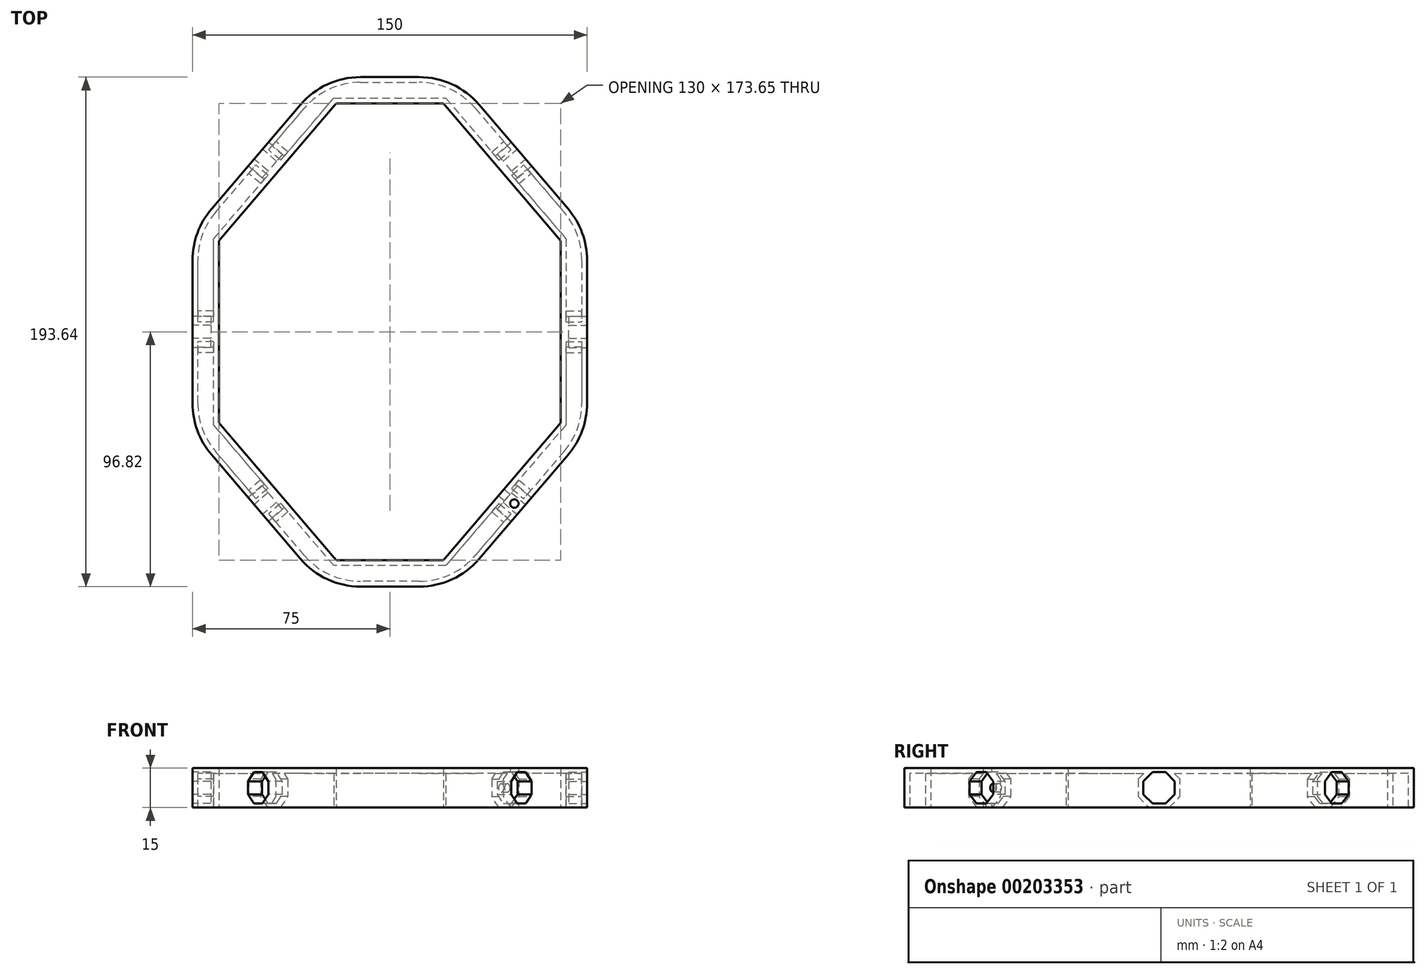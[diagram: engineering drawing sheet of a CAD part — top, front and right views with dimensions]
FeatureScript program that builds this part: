
annotation { "Feature Type Name" : "Feature", "Feature Type Description" : "" }
export const myFeature = defineFeature(function(context is Context, id is Id, definition is map)
    precondition{}
    {
        {
            var Q0;
            Q0=qCreatedBy(makeId("Front.planeOp"),FACE);
            var sketch = newSketch(context, id + "F0", { "sketchPlane" : qUnion([Q0])});
            skPoint(sketch, "E0.endSnap0", {"position": v(0, -12.85) * mm});
            skLineSegment(sketch, "E1", {"start": v(0, 12.85) * mm, "end": v(0, -12.85) * mm, "construction": true});
            skPoint(sketch, "E2", {"position": v(0, 0) * mm});
            skPoint(sketch, "E3", {"position": v(-5.95, 6.72) * mm});
            skPoint(sketch, "E4", {"position": v(-5.95, -6.72) * mm});
            skPoint(sketch, "E5", {"position": v(5.95, 6.72) * mm});
            skPoint(sketch, "E6", {"position": v(5.95, -6.72) * mm});
            skCircle(sketch, "E7.cCircle", {"center": v(0, 0) * mm, "radius": 9.7 * mm, "construction": true});
            skLineSegment(sketch, "E7.0", {"start": v(-8.96, 3.71) * mm, "end": v(-3.71, 8.96) * mm});
            skLineSegment(sketch, "E7.1", {"start": v(-3.71, 8.96) * mm, "end": v(3.71, 8.96) * mm});
            skLineSegment(sketch, "E7.2", {"start": v(3.71, 8.96) * mm, "end": v(8.96, 3.71) * mm});
            skLineSegment(sketch, "E7.3", {"start": v(8.96, 3.71) * mm, "end": v(8.96, -3.71) * mm});
            skLineSegment(sketch, "E7.4", {"start": v(8.96, -3.71) * mm, "end": v(3.71, -8.96) * mm});
            skLineSegment(sketch, "E7.5", {"start": v(3.71, -8.96) * mm, "end": v(-3.71, -8.96) * mm});
            skLineSegment(sketch, "E7.6", {"start": v(-3.71, -8.96) * mm, "end": v(-8.96, -3.71) * mm});
            skLineSegment(sketch, "E7.7", {"start": v(-8.96, -3.71) * mm, "end": v(-8.96, 3.71) * mm});
            skLineSegment(sketch, "E8.0", {"start": v(5.96, -2.47) * mm, "end": v(2.47, -5.96) * mm});
            skLineSegment(sketch, "E8.1", {"start": v(5.96, 2.47) * mm, "end": v(5.96, -2.47) * mm});
            skLineSegment(sketch, "E8.2", {"start": v(2.47, -5.96) * mm, "end": v(-2.47, -5.96) * mm});
            skLineSegment(sketch, "E8.3", {"start": v(2.47, 5.96) * mm, "end": v(5.96, 2.47) * mm});
            skLineSegment(sketch, "E8.4", {"start": v(-2.47, -5.96) * mm, "end": v(-5.96, -2.47) * mm});
            skLineSegment(sketch, "E8.5", {"start": v(-5.96, -2.47) * mm, "end": v(-5.96, 2.47) * mm});
            skLineSegment(sketch, "E8.6", {"start": v(-5.96, 2.47) * mm, "end": v(-2.47, 5.96) * mm});
            skLineSegment(sketch, "E8.7", {"start": v(-2.47, 5.96) * mm, "end": v(2.47, 5.96) * mm});
            skSolve(sketch);
        }
        {
            var Q0;
            Q0=qCreatedBy(makeId("Top.planeOp"),FACE);
            var sketch = newSketch(context, id + "F1", { "sketchPlane" : qUnion([Q0])});
            skLineSegment(sketch, "E9.0", {"start": v(-25, -96.82) * mm, "end": v(-75, -38.27) * mm});
            skLineSegment(sketch, "E9.1", {"start": v(-75, -38.27) * mm, "end": v(-75, 38.27) * mm});
            skLineSegment(sketch, "E9.2", {"start": v(-75, 38.27) * mm, "end": v(-25, 96.82) * mm});
            skLineSegment(sketch, "E9.3", {"start": v(-25, 96.82) * mm, "end": v(25, 96.82) * mm});
            skLineSegment(sketch, "E9.4", {"start": v(25, 96.82) * mm, "end": v(75, 38.27) * mm});
            skLineSegment(sketch, "E9.5", {"start": v(75, 38.27) * mm, "end": v(75, -38.27) * mm});
            skLineSegment(sketch, "E9.6", {"start": v(75, -38.27) * mm, "end": v(25, -96.82) * mm});
            skLineSegment(sketch, "E9.7", {"start": v(25, -96.82) * mm, "end": v(-25, -96.82) * mm});
            skLineSegment(sketch, "E10", {"start": v(0, 138.75) * mm, "end": v(0, -143.6) * mm, "construction": true});
            skPoint(sketch, "E11", {"position": v(0, 96.82) * mm});
            skPoint(sketch, "E12", {"position": v(0, -96.82) * mm});
            skLineSegment(sketch, "E13", {"start": v(-114.22, 0) * mm, "end": v(128.87, 0) * mm, "construction": true});
            skPoint(sketch, "E14", {"position": v(-75, 0) * mm});
            skPoint(sketch, "E15", {"position": v(75, 0) * mm});
            skLineSegment(sketch, "E16.0", {"start": v(65, 34.58) * mm, "end": v(65, -34.58) * mm});
            skLineSegment(sketch, "E16.1", {"start": v(20.39, 86.82) * mm, "end": v(65, 34.58) * mm});
            skLineSegment(sketch, "E16.2", {"start": v(65, -34.58) * mm, "end": v(20.39, -86.82) * mm});
            skLineSegment(sketch, "E16.3", {"start": v(-20.39, 86.82) * mm, "end": v(20.39, 86.82) * mm});
            skLineSegment(sketch, "E16.4", {"start": v(20.39, -86.82) * mm, "end": v(-20.39, -86.82) * mm});
            skLineSegment(sketch, "E16.5", {"start": v(-20.39, -86.82) * mm, "end": v(-65, -34.58) * mm});
            skLineSegment(sketch, "E16.6", {"start": v(-65, -34.58) * mm, "end": v(-65, 34.58) * mm});
            skLineSegment(sketch, "E16.7", {"start": v(-65, 34.58) * mm, "end": v(-20.39, 86.82) * mm});
            skSolve(sketch);
        }
        {
            var Q0;
            Q0=makeQuery(id+"F1.imprint","IMPRINT",FACE,{"disambiguationData":[TD([[makeQuery(id+"F1.imprint","IMPRINT",EDGE,{"derivedFrom":sQuery(id+"F1.wireOp",EDGE,"E9.0")}),-1.0]])]});
            extrude(context, id + "F2", {"entities" : qUnion([Q0]), "depth" : 15 * mm});
        }
        {
            var Q0;
            Q0=makeQuery(id+"F2.opExtrude","SWEPT_FACE",FACE,{"disambiguationData":[OSD([sQuery(id+"F1.wireOp",EDGE,"E9.4")])]});
            var sketch = newSketch(context, id + "F3", { "sketchPlane" : qUnion([Q0])});
            skPoint(sketch, "E17.endSnap0", {"position": v(18.9, 0) * mm});
            skLineSegment(sketch, "E18", {"start": v(18.9, 15) * mm, "end": v(18.9, 0) * mm, "construction": true});
            skPoint(sketch, "E19", {"position": v(18.9, 7.5) * mm});
            skPoint(sketch, "E20", {"position": v(12.95, 14.22) * mm});
            skPoint(sketch, "E21", {"position": v(12.94, 0.78) * mm});
            skPoint(sketch, "E22", {"position": v(24.85, 14.22) * mm});
            skPoint(sketch, "E23", {"position": v(24.85, 0.78) * mm});
            skCircle(sketch, "E24.cCircle", {"center": v(18.9, 7.5) * mm, "radius": 9.7 * mm, "construction": true});
            skLineSegment(sketch, "E24.0", {"start": v(9.94, 11.21) * mm, "end": v(15.19, 16.46) * mm});
            skLineSegment(sketch, "E24.1", {"start": v(15.19, 16.46) * mm, "end": v(22.61, 16.46) * mm});
            skLineSegment(sketch, "E24.2", {"start": v(22.61, 16.46) * mm, "end": v(27.86, 11.21) * mm});
            skLineSegment(sketch, "E24.3", {"start": v(27.86, 11.21) * mm, "end": v(27.86, 3.79) * mm});
            skLineSegment(sketch, "E24.4", {"start": v(27.86, 3.79) * mm, "end": v(22.61, -1.46) * mm});
            skLineSegment(sketch, "E24.5", {"start": v(22.61, -1.46) * mm, "end": v(15.19, -1.46) * mm});
            skLineSegment(sketch, "E24.6", {"start": v(15.19, -1.46) * mm, "end": v(9.94, 3.79) * mm});
            skLineSegment(sketch, "E24.7", {"start": v(9.94, 3.79) * mm, "end": v(9.94, 11.21) * mm});
            skLineSegment(sketch, "E25.0", {"start": v(24.86, 5.03) * mm, "end": v(21.37, 1.54) * mm});
            skLineSegment(sketch, "E25.1", {"start": v(24.86, 9.97) * mm, "end": v(24.86, 5.03) * mm});
            skLineSegment(sketch, "E25.2", {"start": v(21.37, 1.54) * mm, "end": v(16.43, 1.54) * mm});
            skLineSegment(sketch, "E25.3", {"start": v(21.37, 13.46) * mm, "end": v(24.86, 9.97) * mm});
            skLineSegment(sketch, "E25.4", {"start": v(16.43, 1.54) * mm, "end": v(12.94, 5.03) * mm});
            skLineSegment(sketch, "E25.5", {"start": v(12.94, 5.03) * mm, "end": v(12.94, 9.97) * mm});
            skLineSegment(sketch, "E25.6", {"start": v(12.94, 9.97) * mm, "end": v(16.43, 13.46) * mm});
            skLineSegment(sketch, "E25.7", {"start": v(16.43, 13.46) * mm, "end": v(21.37, 13.46) * mm});
            skSolve(sketch);
        }
        {
            var Q0;
            Q0=makeQuery(id+"F3.imprint","IMPRINT",FACE,{"disambiguationData":[TD([[makeQuery(id+"F3.imprint","IMPRINT",EDGE,{"derivedFrom":sQuery(id+"F3.wireOp",EDGE,"E25.0")}),-1.0]])]});
            extrude(context, id + "F4", {"entities" : qUnion([Q0]), "operationType" : NewBodyOperationType.REMOVE, "oppositeDirection" : true, "depth" : 7 * mm});
        }
        {
            var Q0;
            Q0=makeQuery(id+"F2.opExtrude","SWEPT_FACE",FACE,{"disambiguationData":[OSD([sQuery(id+"F1.wireOp",EDGE,"E9.5")])]});
            var sketch = newSketch(context, id + "F5", { "sketchPlane" : qUnion([Q0])});
            skPoint(sketch, "E26.endSnap0", {"position": v(0, 0) * mm});
            skLineSegment(sketch, "E27", {"start": v(0, 15) * mm, "end": v(0, 0) * mm, "construction": true});
            skPoint(sketch, "E28", {"position": v(0, 7.5) * mm});
            skPoint(sketch, "E29", {"position": v(-5.95, 14.22) * mm});
            skPoint(sketch, "E30", {"position": v(-5.95, 0.78) * mm});
            skPoint(sketch, "E31", {"position": v(5.95, 14.22) * mm});
            skPoint(sketch, "E32", {"position": v(5.95, 0.78) * mm});
            skCircle(sketch, "E33.cCircle", {"center": v(0, 7.5) * mm, "radius": 9.7 * mm, "construction": true});
            skLineSegment(sketch, "E33.0", {"start": v(-8.96, 11.21) * mm, "end": v(-3.71, 16.46) * mm});
            skLineSegment(sketch, "E33.1", {"start": v(-3.71, 16.46) * mm, "end": v(3.71, 16.46) * mm});
            skLineSegment(sketch, "E33.2", {"start": v(3.71, 16.46) * mm, "end": v(8.96, 11.21) * mm});
            skLineSegment(sketch, "E33.3", {"start": v(8.96, 11.21) * mm, "end": v(8.96, 3.79) * mm});
            skLineSegment(sketch, "E33.4", {"start": v(8.96, 3.79) * mm, "end": v(3.71, -1.46) * mm});
            skLineSegment(sketch, "E33.5", {"start": v(3.71, -1.46) * mm, "end": v(-3.71, -1.46) * mm});
            skLineSegment(sketch, "E33.6", {"start": v(-3.71, -1.46) * mm, "end": v(-8.96, 3.79) * mm});
            skLineSegment(sketch, "E33.7", {"start": v(-8.96, 3.79) * mm, "end": v(-8.96, 11.21) * mm});
            skLineSegment(sketch, "E34.0", {"start": v(5.96, 5.03) * mm, "end": v(2.47, 1.54) * mm});
            skLineSegment(sketch, "E34.1", {"start": v(5.96, 9.97) * mm, "end": v(5.96, 5.03) * mm});
            skLineSegment(sketch, "E34.2", {"start": v(2.47, 1.54) * mm, "end": v(-2.47, 1.54) * mm});
            skLineSegment(sketch, "E34.3", {"start": v(2.47, 13.46) * mm, "end": v(5.96, 9.97) * mm});
            skLineSegment(sketch, "E34.4", {"start": v(-2.47, 1.54) * mm, "end": v(-5.96, 5.03) * mm});
            skLineSegment(sketch, "E34.5", {"start": v(-5.96, 5.03) * mm, "end": v(-5.96, 9.97) * mm});
            skLineSegment(sketch, "E34.6", {"start": v(-5.96, 9.97) * mm, "end": v(-2.47, 13.46) * mm});
            skLineSegment(sketch, "E34.7", {"start": v(-2.47, 13.46) * mm, "end": v(2.47, 13.46) * mm});
            skSolve(sketch);
        }
        {
            var Q0;
            Q0=makeQuery(id+"F2.opExtrude","SWEPT_FACE",FACE,{"disambiguationData":[OSD([sQuery(id+"F1.wireOp",EDGE,"E9.6")])]});
            var sketch = newSketch(context, id + "F6", { "sketchPlane" : qUnion([Q0])});
            skPoint(sketch, "E35.endSnap0", {"position": v(-18.9, 0) * mm});
            skLineSegment(sketch, "E36", {"start": v(-18.9, 15) * mm, "end": v(-18.9, 0) * mm, "construction": true});
            skPoint(sketch, "E37", {"position": v(-18.9, 7.5) * mm});
            skPoint(sketch, "E38", {"position": v(-24.85, 14.22) * mm});
            skPoint(sketch, "E39", {"position": v(-24.85, 0.78) * mm});
            skPoint(sketch, "E40", {"position": v(-12.95, 14.22) * mm});
            skPoint(sketch, "E41", {"position": v(-12.95, 0.78) * mm});
            skCircle(sketch, "E42.cCircle", {"center": v(-18.9, 7.5) * mm, "radius": 9.7 * mm, "construction": true});
            skLineSegment(sketch, "E42.0", {"start": v(-27.86, 11.21) * mm, "end": v(-22.61, 16.46) * mm});
            skLineSegment(sketch, "E42.1", {"start": v(-22.61, 16.46) * mm, "end": v(-15.19, 16.46) * mm});
            skLineSegment(sketch, "E42.2", {"start": v(-15.19, 16.46) * mm, "end": v(-9.94, 11.21) * mm});
            skLineSegment(sketch, "E42.3", {"start": v(-9.94, 11.21) * mm, "end": v(-9.94, 3.79) * mm});
            skLineSegment(sketch, "E42.4", {"start": v(-9.94, 3.79) * mm, "end": v(-15.19, -1.46) * mm});
            skLineSegment(sketch, "E42.5", {"start": v(-15.19, -1.46) * mm, "end": v(-22.61, -1.46) * mm});
            skLineSegment(sketch, "E42.6", {"start": v(-22.61, -1.46) * mm, "end": v(-27.86, 3.79) * mm});
            skLineSegment(sketch, "E42.7", {"start": v(-27.86, 3.79) * mm, "end": v(-27.86, 11.21) * mm});
            skLineSegment(sketch, "E43.0", {"start": v(-12.94, 5.03) * mm, "end": v(-16.43, 1.54) * mm});
            skLineSegment(sketch, "E43.1", {"start": v(-12.94, 9.97) * mm, "end": v(-12.94, 5.03) * mm});
            skLineSegment(sketch, "E43.2", {"start": v(-16.43, 1.54) * mm, "end": v(-21.37, 1.54) * mm});
            skLineSegment(sketch, "E43.3", {"start": v(-16.43, 13.46) * mm, "end": v(-12.94, 9.97) * mm});
            skLineSegment(sketch, "E43.4", {"start": v(-21.37, 1.54) * mm, "end": v(-24.86, 5.03) * mm});
            skLineSegment(sketch, "E43.5", {"start": v(-24.86, 5.03) * mm, "end": v(-24.86, 9.97) * mm});
            skLineSegment(sketch, "E43.6", {"start": v(-24.86, 9.97) * mm, "end": v(-21.37, 13.46) * mm});
            skLineSegment(sketch, "E43.7", {"start": v(-21.37, 13.46) * mm, "end": v(-16.43, 13.46) * mm});
            skCircle(sketch, "E44", {"center": v(-18.9, 7.5) * mm, "radius": 1.6 * mm});
            skSolve(sketch);
        }
        {
            var Q0;
            Q0=makeQuery(id+"F2.opExtrude","SWEPT_FACE",FACE,{"disambiguationData":[OSD([sQuery(id+"F1.wireOp",EDGE,"E9.2")])]});
            var sketch = newSketch(context, id + "F7", { "sketchPlane" : qUnion([Q0])});
            skPoint(sketch, "E45.endSnap0", {"position": v(-18.9, 0) * mm});
            skLineSegment(sketch, "E46", {"start": v(-18.9, 15) * mm, "end": v(-18.9, 0) * mm, "construction": true});
            skPoint(sketch, "E47", {"position": v(-18.9, 7.5) * mm});
            skPoint(sketch, "E48", {"position": v(-24.85, 14.22) * mm});
            skPoint(sketch, "E49", {"position": v(-24.85, 0.78) * mm});
            skPoint(sketch, "E50", {"position": v(-12.95, 14.22) * mm});
            skPoint(sketch, "E51", {"position": v(-12.95, 0.78) * mm});
            skCircle(sketch, "E52.cCircle", {"center": v(-18.9, 7.5) * mm, "radius": 9.7 * mm, "construction": true});
            skLineSegment(sketch, "E52.0", {"start": v(-27.86, 11.21) * mm, "end": v(-22.61, 16.46) * mm});
            skLineSegment(sketch, "E52.1", {"start": v(-22.61, 16.46) * mm, "end": v(-15.19, 16.46) * mm});
            skLineSegment(sketch, "E52.2", {"start": v(-15.19, 16.46) * mm, "end": v(-9.94, 11.21) * mm});
            skLineSegment(sketch, "E52.3", {"start": v(-9.94, 11.21) * mm, "end": v(-9.94, 3.79) * mm});
            skLineSegment(sketch, "E52.4", {"start": v(-9.94, 3.79) * mm, "end": v(-15.19, -1.46) * mm});
            skLineSegment(sketch, "E52.5", {"start": v(-15.19, -1.46) * mm, "end": v(-22.61, -1.46) * mm});
            skLineSegment(sketch, "E52.6", {"start": v(-22.61, -1.46) * mm, "end": v(-27.86, 3.79) * mm});
            skLineSegment(sketch, "E52.7", {"start": v(-27.86, 3.79) * mm, "end": v(-27.86, 11.21) * mm});
            skLineSegment(sketch, "E53.0", {"start": v(-12.94, 5.03) * mm, "end": v(-16.43, 1.54) * mm});
            skLineSegment(sketch, "E53.1", {"start": v(-12.94, 9.97) * mm, "end": v(-12.94, 5.03) * mm});
            skLineSegment(sketch, "E53.2", {"start": v(-16.43, 1.54) * mm, "end": v(-21.37, 1.54) * mm});
            skLineSegment(sketch, "E53.3", {"start": v(-16.43, 13.46) * mm, "end": v(-12.94, 9.97) * mm});
            skLineSegment(sketch, "E53.4", {"start": v(-21.37, 1.54) * mm, "end": v(-24.86, 5.03) * mm});
            skLineSegment(sketch, "E53.5", {"start": v(-24.86, 5.03) * mm, "end": v(-24.86, 9.97) * mm});
            skLineSegment(sketch, "E53.6", {"start": v(-24.86, 9.97) * mm, "end": v(-21.37, 13.46) * mm});
            skLineSegment(sketch, "E53.7", {"start": v(-21.37, 13.46) * mm, "end": v(-16.43, 13.46) * mm});
            skSolve(sketch);
        }
        {
            var Q0;
            Q0=makeQuery(id+"F2.opExtrude","SWEPT_FACE",FACE,{"disambiguationData":[OSD([sQuery(id+"F1.wireOp",EDGE,"E9.1")])]});
            var sketch = newSketch(context, id + "F8", { "sketchPlane" : qUnion([Q0])});
            skPoint(sketch, "E54.endSnap0", {"position": v(0, 0) * mm});
            skLineSegment(sketch, "E55", {"start": v(0, 15) * mm, "end": v(0, 0) * mm, "construction": true});
            skPoint(sketch, "E56", {"position": v(0, 7.5) * mm});
            skPoint(sketch, "E57", {"position": v(-5.95, 14.22) * mm});
            skPoint(sketch, "E58", {"position": v(-5.96, 0.78) * mm});
            skPoint(sketch, "E59", {"position": v(5.95, 14.22) * mm});
            skPoint(sketch, "E60", {"position": v(5.95, 0.78) * mm});
            skCircle(sketch, "E61.cCircle", {"center": v(0, 7.5) * mm, "radius": 9.7 * mm, "construction": true});
            skLineSegment(sketch, "E61.0", {"start": v(-8.96, 11.21) * mm, "end": v(-3.71, 16.46) * mm});
            skLineSegment(sketch, "E61.1", {"start": v(-3.71, 16.46) * mm, "end": v(3.71, 16.46) * mm});
            skLineSegment(sketch, "E61.2", {"start": v(3.71, 16.46) * mm, "end": v(8.96, 11.21) * mm});
            skLineSegment(sketch, "E61.3", {"start": v(8.96, 11.21) * mm, "end": v(8.96, 3.79) * mm});
            skLineSegment(sketch, "E61.4", {"start": v(8.96, 3.79) * mm, "end": v(3.71, -1.46) * mm});
            skLineSegment(sketch, "E61.5", {"start": v(3.71, -1.46) * mm, "end": v(-3.71, -1.46) * mm});
            skLineSegment(sketch, "E61.6", {"start": v(-3.71, -1.46) * mm, "end": v(-8.96, 3.79) * mm});
            skLineSegment(sketch, "E61.7", {"start": v(-8.96, 3.79) * mm, "end": v(-8.96, 11.21) * mm});
            skLineSegment(sketch, "E62.0", {"start": v(5.96, 5.03) * mm, "end": v(2.47, 1.54) * mm});
            skLineSegment(sketch, "E62.1", {"start": v(5.96, 9.97) * mm, "end": v(5.96, 5.03) * mm});
            skLineSegment(sketch, "E62.2", {"start": v(2.47, 1.54) * mm, "end": v(-2.47, 1.54) * mm});
            skLineSegment(sketch, "E62.3", {"start": v(2.47, 13.46) * mm, "end": v(5.96, 9.97) * mm});
            skLineSegment(sketch, "E62.4", {"start": v(-2.47, 1.54) * mm, "end": v(-5.96, 5.03) * mm});
            skLineSegment(sketch, "E62.5", {"start": v(-5.96, 5.03) * mm, "end": v(-5.96, 9.97) * mm});
            skLineSegment(sketch, "E62.6", {"start": v(-5.96, 9.97) * mm, "end": v(-2.47, 13.46) * mm});
            skLineSegment(sketch, "E62.7", {"start": v(-2.47, 13.46) * mm, "end": v(2.47, 13.46) * mm});
            skSolve(sketch);
        }
        {
            var Q0;
            Q0=makeQuery(id+"F2.opExtrude","SWEPT_FACE",FACE,{"disambiguationData":[OSD([sQuery(id+"F1.wireOp",EDGE,"E9.0")])]});
            var sketch = newSketch(context, id + "F9", { "sketchPlane" : qUnion([Q0])});
            skPoint(sketch, "E63.endSnap0", {"position": v(18.9, 0) * mm});
            skLineSegment(sketch, "E64", {"start": v(18.9, 15) * mm, "end": v(18.9, 0) * mm, "construction": true});
            skPoint(sketch, "E65", {"position": v(18.9, 7.5) * mm});
            skPoint(sketch, "E66", {"position": v(12.95, 14.22) * mm});
            skPoint(sketch, "E67", {"position": v(12.94, 0.78) * mm});
            skPoint(sketch, "E68", {"position": v(24.85, 14.22) * mm});
            skPoint(sketch, "E69", {"position": v(24.85, 0.78) * mm});
            skCircle(sketch, "E70.cCircle", {"center": v(18.9, 7.5) * mm, "radius": 9.7 * mm, "construction": true});
            skLineSegment(sketch, "E70.0", {"start": v(9.94, 11.21) * mm, "end": v(15.19, 16.46) * mm});
            skLineSegment(sketch, "E70.1", {"start": v(15.19, 16.46) * mm, "end": v(22.61, 16.46) * mm});
            skLineSegment(sketch, "E70.2", {"start": v(22.61, 16.46) * mm, "end": v(27.86, 11.21) * mm});
            skLineSegment(sketch, "E70.3", {"start": v(27.86, 11.21) * mm, "end": v(27.86, 3.79) * mm});
            skLineSegment(sketch, "E70.4", {"start": v(27.86, 3.79) * mm, "end": v(22.61, -1.46) * mm});
            skLineSegment(sketch, "E70.5", {"start": v(22.61, -1.46) * mm, "end": v(15.19, -1.46) * mm});
            skLineSegment(sketch, "E70.6", {"start": v(15.19, -1.46) * mm, "end": v(9.94, 3.79) * mm});
            skLineSegment(sketch, "E70.7", {"start": v(9.94, 3.79) * mm, "end": v(9.94, 11.21) * mm});
            skLineSegment(sketch, "E71.0", {"start": v(24.86, 5.03) * mm, "end": v(21.37, 1.54) * mm});
            skLineSegment(sketch, "E71.1", {"start": v(24.86, 9.97) * mm, "end": v(24.86, 5.03) * mm});
            skLineSegment(sketch, "E71.2", {"start": v(21.37, 1.54) * mm, "end": v(16.43, 1.54) * mm});
            skLineSegment(sketch, "E71.3", {"start": v(21.37, 13.46) * mm, "end": v(24.86, 9.97) * mm});
            skLineSegment(sketch, "E71.4", {"start": v(16.43, 1.54) * mm, "end": v(12.94, 5.03) * mm});
            skLineSegment(sketch, "E71.5", {"start": v(12.94, 5.03) * mm, "end": v(12.94, 9.97) * mm});
            skLineSegment(sketch, "E71.6", {"start": v(12.94, 9.97) * mm, "end": v(16.43, 13.46) * mm});
            skLineSegment(sketch, "E71.7", {"start": v(16.43, 13.46) * mm, "end": v(21.37, 13.46) * mm});
            skSolve(sketch);
        }
        {
            var Q0;
            Q0=makeQuery(id+"F7.imprint","IMPRINT",FACE,{"disambiguationData":[TD([[makeQuery(id+"F7.imprint","IMPRINT",EDGE,{"derivedFrom":sQuery(id+"F7.wireOp",EDGE,"E53.0")}),-1.0]])]});
            extrude(context, id + "F10", {"entities" : qUnion([Q0]), "operationType" : NewBodyOperationType.REMOVE, "oppositeDirection" : true, "depth" : 7 * mm});
        }
        {
            var Q0;
            Q0=makeQuery(id+"F8.imprint","IMPRINT",FACE,{"disambiguationData":[TD([[makeQuery(id+"F8.imprint","IMPRINT",EDGE,{"derivedFrom":sQuery(id+"F8.wireOp",EDGE,"E62.0")}),-1.0]])]});
            extrude(context, id + "F11", {"entities" : qUnion([Q0]), "operationType" : NewBodyOperationType.REMOVE, "oppositeDirection" : true, "depth" : 7 * mm});
        }
        {
            var Q0;
            Q0=makeQuery(id+"F9.imprint","IMPRINT",FACE,{"disambiguationData":[TD([[makeQuery(id+"F9.imprint","IMPRINT",EDGE,{"derivedFrom":sQuery(id+"F9.wireOp",EDGE,"E71.0")}),-1.0]])]});
            extrude(context, id + "F12", {"entities" : qUnion([Q0]), "operationType" : NewBodyOperationType.REMOVE, "oppositeDirection" : true, "depth" : 7 * mm});
        }
        {
            var Q0;
            Q0=makeQuery(id+"F6.imprint","IMPRINT",FACE,{"disambiguationData":[TD([[makeQuery(id+"F6.imprint","IMPRINT",EDGE,{"derivedFrom":sQuery(id+"F6.wireOp",EDGE,"E43.0")}),-1.0]])]});
            var Q1;
            Q1=makeQuery(id+"F6.imprint","IMPRINT",FACE,{"disambiguationData":[TD([[makeQuery(id+"F6.imprint","IMPRINT",EDGE,{"derivedFrom":sQuery(id+"F6.wireOp",EDGE,"E44")}),1.0]])]});
            extrude(context, id + "F13", {"entities" : qUnion([Q0, Q1]), "operationType" : NewBodyOperationType.REMOVE, "oppositeDirection" : true, "depth" : 7 * mm});
        }
        {
            var Q0;
            Q0=makeQuery(id+"F5.imprint","IMPRINT",FACE,{"disambiguationData":[TD([[makeQuery(id+"F5.imprint","IMPRINT",EDGE,{"derivedFrom":sQuery(id+"F5.wireOp",EDGE,"E34.0")}),-1.0]])]});
            extrude(context, id + "F14", {"entities" : qUnion([Q0]), "operationType" : NewBodyOperationType.REMOVE, "oppositeDirection" : true, "depth" : 7 * mm});
        }
        {
            var Q0;
            Q0=makeQuery(id+"F1.imprint","IMPRINT",FACE,{"disambiguationData":[TD([[makeQuery(id+"F1.imprint","IMPRINT",EDGE,{"derivedFrom":sQuery(id+"F1.wireOp",EDGE,"E9.0")}),-1.0]])]});
            var sketch = newSketch(context, id + "F15", { "sketchPlane" : qUnion([Q0])});
            skLineSegment(sketch, "E72", {"start": v(50, -67.55) * mm, "end": v(44.68, -63) * mm, "construction": true});
            skPoint(sketch, "E73", {"position": v(47.34, -65.27) * mm});
            skCircle(sketch, "E74", {"center": v(47.34, -65.27) * mm, "radius": 1.6 * mm});
            skCircle(sketch, "E75", {"center": v(47.34, -65.27) * mm, "radius": 15.5 * mm});
            skSolve(sketch);
        }
        {
            var Q0;
            Q0=makeQuery(id+"F15.imprint","IMPRINT",FACE,{"disambiguationData":[TD([[makeQuery(id+"F15.imprint","IMPRINT",EDGE,{"derivedFrom":sQuery(id+"F15.wireOp",EDGE,"E74")}),1.0]])]});
            extrude(context, id + "F16", {"entities" : qUnion([Q0]), "operationType" : NewBodyOperationType.REMOVE, "depth" : 25 * mm});
        }
        {
            var Q0;
            Q0=makeQuery(id+"F2.opExtrude","SWEPT_EDGE",EDGE,{"disambiguationData":[OSD([sQuery(id+"F1.wireOp",EDGE,"E9.2"),sQuery(id+"F1.wireOp",EDGE,"E9.3")])]});
            var Q1;
            Q1=makeQuery(id+"F2.opExtrude","SWEPT_EDGE",EDGE,{"disambiguationData":[OSD([sQuery(id+"F1.wireOp",EDGE,"E9.1"),sQuery(id+"F1.wireOp",EDGE,"E9.2")])]});
            var Q2;
            Q2=makeQuery(id+"F2.opExtrude","SWEPT_EDGE",EDGE,{"disambiguationData":[OSD([sQuery(id+"F1.wireOp",EDGE,"E9.0"),sQuery(id+"F1.wireOp",EDGE,"E9.1")])]});
            var Q3;
            Q3=makeQuery(id+"F2.opExtrude","SWEPT_EDGE",EDGE,{"disambiguationData":[OSD([sQuery(id+"F1.wireOp",EDGE,"E9.0"),sQuery(id+"F1.wireOp",EDGE,"E9.7")])]});
            var Q4;
            Q4=makeQuery(id+"F2.opExtrude","SWEPT_EDGE",EDGE,{"disambiguationData":[OSD([sQuery(id+"F1.wireOp",EDGE,"E9.6"),sQuery(id+"F1.wireOp",EDGE,"E9.7")])]});
            var Q5;
            Q5=makeQuery(id+"F2.opExtrude","SWEPT_EDGE",EDGE,{"disambiguationData":[OSD([sQuery(id+"F1.wireOp",EDGE,"E9.5"),sQuery(id+"F1.wireOp",EDGE,"E9.6")])]});
            var Q6;
            Q6=makeQuery(id+"F2.opExtrude","SWEPT_EDGE",EDGE,{"disambiguationData":[OSD([sQuery(id+"F1.wireOp",EDGE,"E9.4"),sQuery(id+"F1.wireOp",EDGE,"E9.5")])]});
            var Q7;
            Q7=makeQuery(id+"F2.opExtrude","SWEPT_EDGE",EDGE,{"disambiguationData":[OSD([sQuery(id+"F1.wireOp",EDGE,"E9.3"),sQuery(id+"F1.wireOp",EDGE,"E9.4")])]});
            fillet(context, id + "F17", {"entities" : qUnion([Q0, Q1, Q2, Q3, Q4, Q5, Q6, Q7]), "radius" : 30 * mm, "tangentPropagation" : true, "allowEdgeOverflow" : false});
        }
        {
            var Q0;
            Q0=makeQuery(id+"F2.opExtrude","CAP_FACE",FACE,{"disambiguationData":[OSD([sQuery(id+"F1.wireOp",EDGE,"E9.0"),sQuery(id+"F1.wireOp",EDGE,"E9.1"),sQuery(id+"F1.wireOp",EDGE,"E9.2"),sQuery(id+"F1.wireOp",EDGE,"E9.3"),sQuery(id+"F1.wireOp",EDGE,"E9.4"),sQuery(id+"F1.wireOp",EDGE,"E9.5"),sQuery(id+"F1.wireOp",EDGE,"E9.6"),sQuery(id+"F1.wireOp",EDGE,"E9.7")])],"isStart":true});
            var Q1;
            Q1=makeQuery(id+"F2.opExtrude","SWEPT_BODY",BODY,{"disambiguationData":[OSD([sQuery(id+"F1.wireOp",EDGE,"E9.0"),sQuery(id+"F1.wireOp",EDGE,"E9.1"),sQuery(id+"F1.wireOp",EDGE,"E9.2"),sQuery(id+"F1.wireOp",EDGE,"E9.3"),sQuery(id+"F1.wireOp",EDGE,"E9.4"),sQuery(id+"F1.wireOp",EDGE,"E9.5"),sQuery(id+"F1.wireOp",EDGE,"E9.6"),sQuery(id+"F1.wireOp",EDGE,"E9.7")])]});
            shell(context, id + "F18", {"entities" : qUnion([Q0]), "parts" : qUnion([Q1]), "thickness" : 2 * mm});
        }
        {
            var Q0;
            Q0=makeQuery(id+"F6.imprint","IMPRINT",FACE,{"disambiguationData":[TD([[makeQuery(id+"F6.imprint","IMPRINT",EDGE,{"derivedFrom":sQuery(id+"F6.wireOp",EDGE,"E44")}),1.0]])]});
            extrude(context, id + "F19", {"entities" : qUnion([Q0]), "operationType" : NewBodyOperationType.REMOVE, "oppositeDirection" : true, "depth" : 25 * mm});
        }
    });
